# Revit family: Einlegeblech_585_FS_DD_FT_A2
name_source: partatom
category: Generic Models
revit_build: Autodesk Revit 2017 (Build: 20160225_1515(x64)
units: mm (PartAtom-declared; Revit-internal decimal feet)

## family parameters
Always vertical = Yes
Can host rebar = No
Cut with Voids When Loaded = No
Part Type = Normal
Room Calculation Point = No
Round Connector Dimension = Use Diameter
Shared = No
Work Plane-Based = No

## types (6) — shared parameters
Cut's number = 59
Cut's number 2 = 60
Cut's number 3 = 2
Cut's number 4 = 3
Cut's number 5 = 4
Cut's space = 50 mm  [stored 0.164042 ft]
Length = 3000 mm  [stored 9.84252 ft]
Manufacturer = OBO Bettermann
URL = http:/www.obo-bettermann.com
Width = 585 mm  [stored 1.91929 ft]
Width 1 = 293 mm

## per-type parameters (varying)
| type | GTIN | Manufacturer Art.No. | Material |
| ELB-L 60 FS | 4012196421213 | 6103332 | Strip-galvanised |
| ELB-L 60 DD | 4012196029228 | 6103368 | Strip galvanised zinc/aluminium, Double Dip |
| ELB-L 60 FT | 4012196308477 | 6103480 | hot-dip galvanised |
| ELB-L60 A2 | 4012195037415 | 6103630 | Stainless stee,l A2 |
| ELB-L 60 FT SO | 4012196954131 | 7189978 | hot-dip galvanised |
| ELB-L 60 DDK LGR | 4012196505951 | 6103398 | Polyester / epoxy |

note: column(s) folded — value = type name in every type: Article Type

note: [stored X ft] marks values corroborated as IEEE doubles in the binary element streams (Revit-internal decimal feet)

## geometry (parser evidence)
native form markers: Sweep x3
no freeform markers — native parametric forms only
